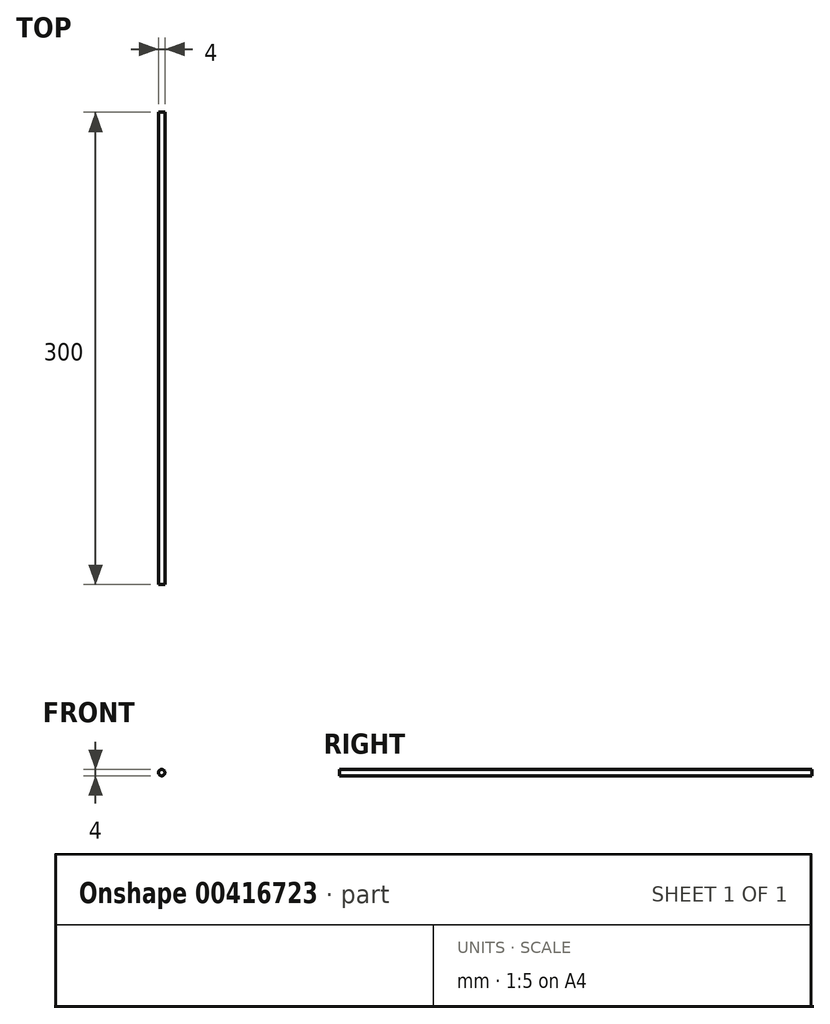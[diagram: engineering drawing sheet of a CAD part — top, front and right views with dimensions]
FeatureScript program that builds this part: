
annotation { "Feature Type Name" : "Feature", "Feature Type Description" : "" }
export const myFeature = defineFeature(function(context is Context, id is Id, definition is map)
    precondition{}
    {
        {
            var Q0;
            Q0=qCreatedBy(makeId("Front.planeOp"),FACE);
            var sketch = newSketch(context, id + "F0", { "sketchPlane" : qUnion([Q0])});
            skCircle(sketch, "E0", {"center": v(0, 0) * mm, "radius": 2 * mm});
            skSolve(sketch);
        }
        {
            var Q0;
            Q0=makeQuery(id+"F0.imprint","IMPRINT",FACE,{"disambiguationData":[TD([[makeQuery(id+"F0.imprint","IMPRINT",EDGE,{"derivedFrom":sQuery(id+"F0.wireOp",EDGE,"E0")}),1.0]])]});
            extrude(context, id + "F1", {"entities" : qUnion([Q0]), "depth" : 300 * mm});
        }
    });
